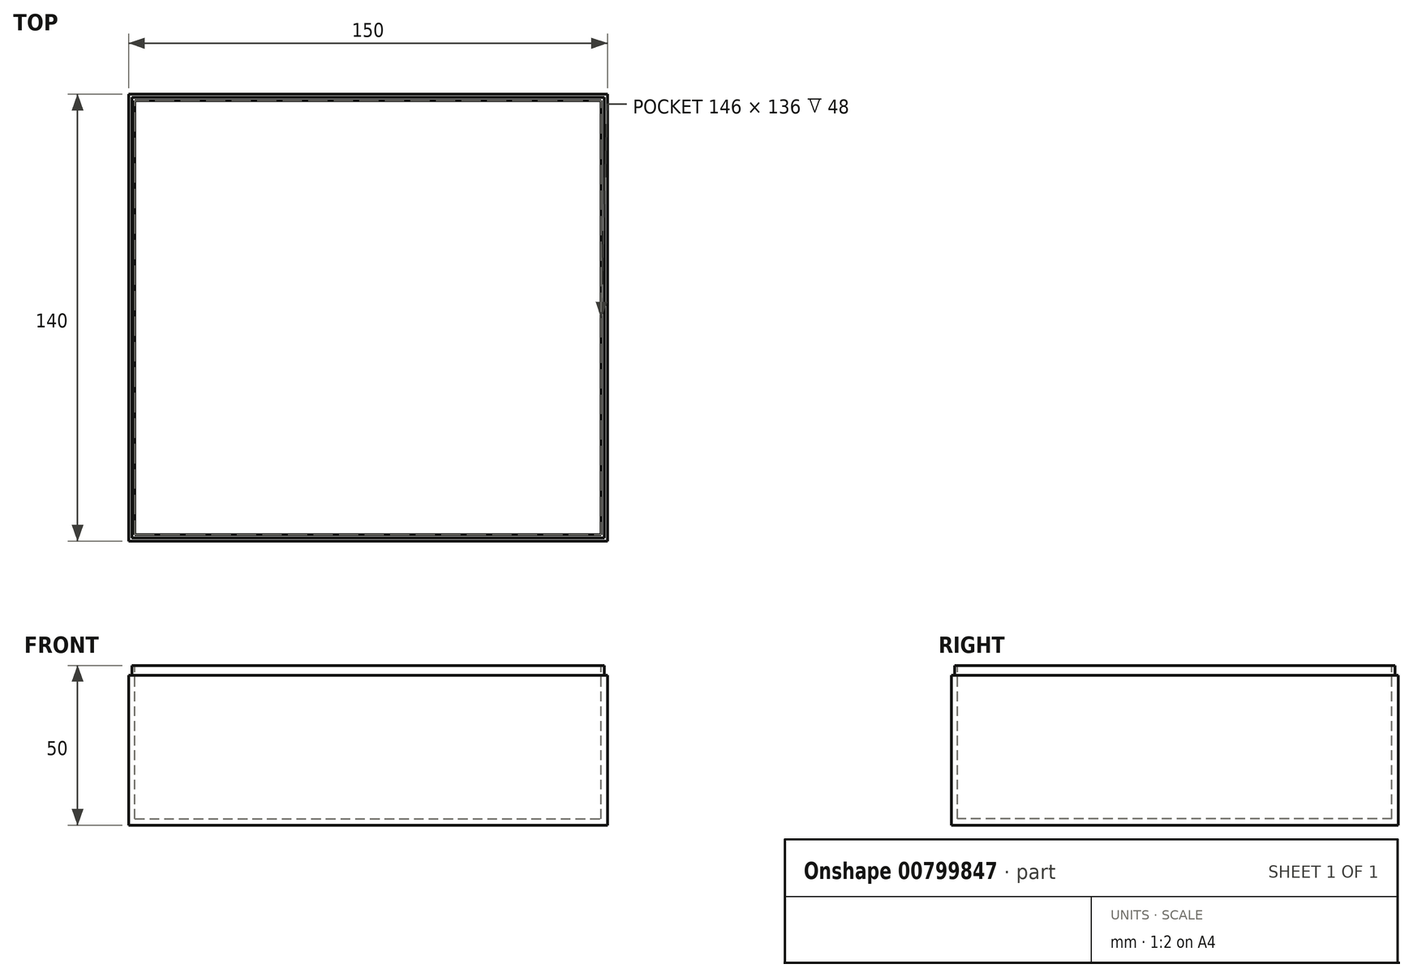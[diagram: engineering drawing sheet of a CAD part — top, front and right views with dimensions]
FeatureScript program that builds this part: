
annotation { "Feature Type Name" : "Feature", "Feature Type Description" : "" }
export const myFeature = defineFeature(function(context is Context, id is Id, definition is map)
    precondition{}
    {
        {
            var Q0;
            Q0=qCreatedBy(makeId("Top.planeOp"),FACE);
            var sketch = newSketch(context, id + "F0", { "sketchPlane" : qUnion([Q0])});
            skLineSegment(sketch, "E0.bottom", {"start": v(2.5, 0) * mm, "end": v(152.5, 0) * mm});
            skLineSegment(sketch, "E0.top", {"start": v(2.5, 140) * mm, "end": v(152.5, 140) * mm});
            skLineSegment(sketch, "E0.left", {"start": v(2.5, 0) * mm, "end": v(2.5, 140) * mm});
            skLineSegment(sketch, "E0.right", {"start": v(152.5, 0) * mm, "end": v(152.5, 140) * mm});
            skSolve(sketch);
        }
        {
            var Q0;
            Q0 = qSketchRegion(id + "F0", true);
            extrude(context, id + "F1", {"entities" : qUnion([Q0]), "depth" : 47 * mm, "offsetDistance" : 25 * mm});
        }
        {
            var Q0;
            Q0=makeQuery(id+"F1.opExtrude","CAP_FACE",FACE,{"disambiguationData":[OSD([sQuery(id+"F0.wireOp",EDGE,"E0.bottom"),sQuery(id+"F0.wireOp",EDGE,"E0.top"),sQuery(id+"F0.wireOp",EDGE,"E0.left"),sQuery(id+"F0.wireOp",EDGE,"E0.right")])],"isStart":false});
            var sketch = newSketch(context, id + "F2", { "sketchPlane" : qUnion([Q0])});
            skLineSegment(sketch, "E1.bottom", {"start": v(4.5, 138) * mm, "end": v(150.5, 138) * mm});
            skLineSegment(sketch, "E1.top", {"start": v(4.5, 2) * mm, "end": v(150.5, 2) * mm});
            skLineSegment(sketch, "E1.left", {"start": v(4.5, 138) * mm, "end": v(4.5, 2) * mm});
            skLineSegment(sketch, "E1.right", {"start": v(150.5, 138) * mm, "end": v(150.5, 2) * mm});
            skSolve(sketch);
        }
        {
            var Q0;
            Q0 = qSketchRegion(id + "F2", true);
            extrude(context, id + "F3", {"entities" : qUnion([Q0]), "operationType" : NewBodyOperationType.REMOVE, "oppositeDirection" : true, "depth" : 45 * mm, "offsetDistance" : 25 * mm});
        }
        {
            var Q0;
            Q0=makeQuery(id+"F1.opExtrude","CAP_FACE",FACE,{"disambiguationData":[OSD([sQuery(id+"F0.wireOp",EDGE,"E0.bottom"),sQuery(id+"F0.wireOp",EDGE,"E0.top"),sQuery(id+"F0.wireOp",EDGE,"E0.left"),sQuery(id+"F0.wireOp",EDGE,"E0.right")])],"isStart":false});
            var sketch = newSketch(context, id + "F4", { "sketchPlane" : qUnion([Q0])});
            skLineSegment(sketch, "E2.bottom", {"start": v(150.5, 138) * mm, "end": v(4.5, 138) * mm});
            skLineSegment(sketch, "E2.top", {"start": v(150.5, 2) * mm, "end": v(4.5, 2) * mm});
            skLineSegment(sketch, "E2.left", {"start": v(150.5, 138) * mm, "end": v(150.5, 2) * mm});
            skLineSegment(sketch, "E2.right", {"start": v(4.5, 138) * mm, "end": v(4.5, 2) * mm});
            skLineSegment(sketch, "E3.bottom", {"start": v(152.5, 140) * mm, "end": v(2.5, 140) * mm});
            skLineSegment(sketch, "E3.top", {"start": v(152.5, 0) * mm, "end": v(2.5, 0) * mm});
            skLineSegment(sketch, "E3.left", {"start": v(152.5, 140) * mm, "end": v(152.5, 0) * mm});
            skLineSegment(sketch, "E3.right", {"start": v(2.5, 140) * mm, "end": v(2.5, 0) * mm});
            skSolve(sketch);
        }
        {
            var Q0;
            Q0 = qSketchRegion(id + "F4", true);
            extrude(context, id + "F5", {"entities" : qUnion([Q0]), "operationType" : NewBodyOperationType.ADD, "depth" : 3 * mm, "offsetDistance" : 25 * mm});
        }
        {
            var Q0;
            Q0=makeQuery(id+"F5.opExtrude","CAP_FACE",FACE,{"disambiguationData":[OSD([sQuery(id+"F4.wireOp",EDGE,"E2.bottom"),sQuery(id+"F4.wireOp",EDGE,"E2.top"),sQuery(id+"F4.wireOp",EDGE,"E2.left"),sQuery(id+"F4.wireOp",EDGE,"E2.right"),sQuery(id+"F4.wireOp",EDGE,"E3.bottom"),sQuery(id+"F4.wireOp",EDGE,"E3.top"),sQuery(id+"F4.wireOp",EDGE,"E3.left"),sQuery(id+"F4.wireOp",EDGE,"E3.right")])],"isStart":false});
            var sketch = newSketch(context, id + "F6", { "sketchPlane" : qUnion([Q0])});
            skLineSegment(sketch, "E4.bottom", {"start": v(151.5, 139) * mm, "end": v(3.5, 139) * mm});
            skLineSegment(sketch, "E4.top", {"start": v(151.5, 1) * mm, "end": v(3.5, 1) * mm});
            skLineSegment(sketch, "E4.left", {"start": v(151.5, 139) * mm, "end": v(151.5, 1) * mm});
            skLineSegment(sketch, "E4.right", {"start": v(3.5, 139) * mm, "end": v(3.5, 1) * mm});
            skSolve(sketch);
        }
        {
            var Q0;
            Q0=makeQuery(id+"F6.imprint","IMPRINT",FACE,{"disambiguationData":[TD([[makeQuery(id+"F6.imprint","IMPRINT",EDGE,{"derivedFrom":sQuery(id+"F6.wireOp",EDGE,"E4.bottom")}),-1.0]])]});
            extrude(context, id + "F7", {"entities" : qUnion([Q0]), "operationType" : NewBodyOperationType.REMOVE, "oppositeDirection" : true, "depth" : 3 * mm, "offsetDistance" : 25 * mm});
        }
    });
